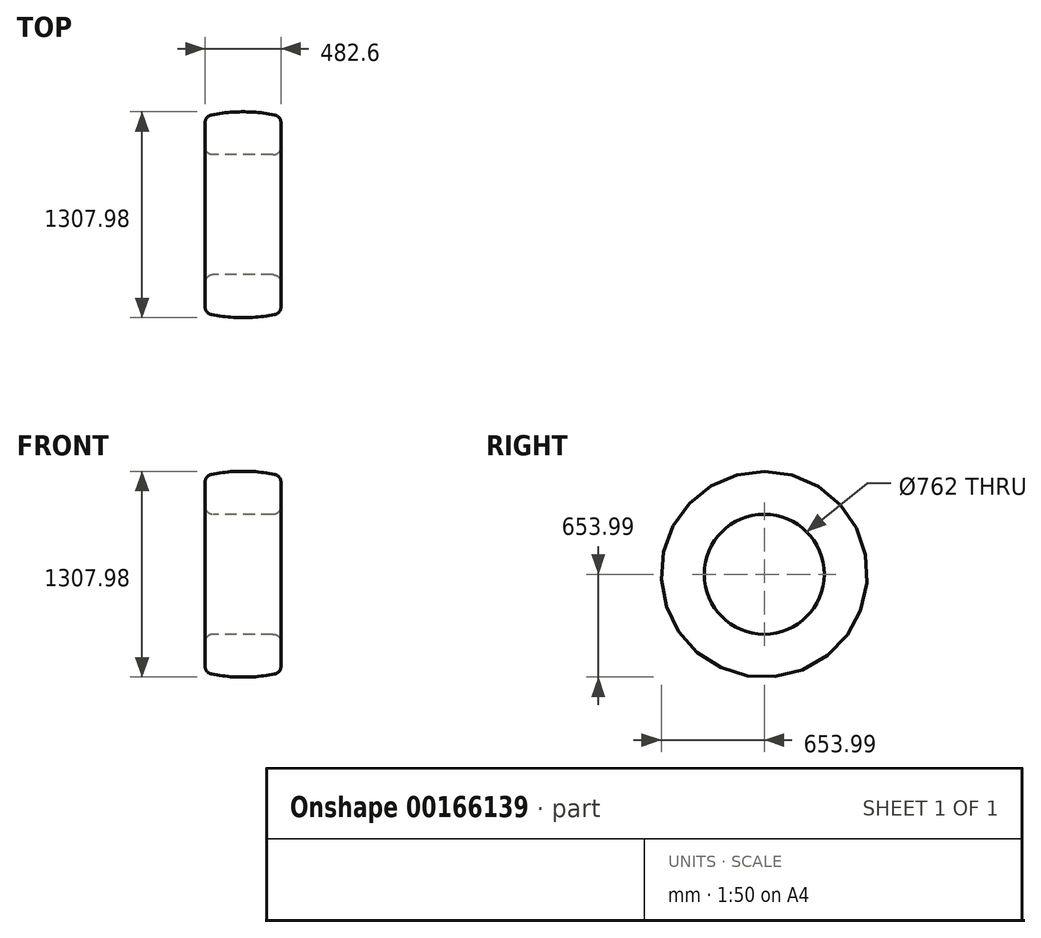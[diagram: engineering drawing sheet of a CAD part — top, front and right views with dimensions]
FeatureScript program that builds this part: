
annotation { "Feature Type Name" : "Feature", "Feature Type Description" : "" }
export const myFeature = defineFeature(function(context is Context, id is Id, definition is map)
    precondition{}
    {
        {
            var Q0;
            Q0=qCreatedBy(makeId("Front.planeOp"),FACE);
            var sketch = newSketch(context, id + "F0", { "sketchPlane" : qUnion([Q0])});
            skLineSegment(sketch, "E0.top", {"start": v(1079.5, -762) * mm, "end": v(1460.5, -762) * mm});
            skLineSegment(sketch, "E0.left", {"start": v(1028.7, -558.8) * mm, "end": v(1028.7, -711.2) * mm});
            skLineSegment(sketch, "E0.right", {"start": v(1511.3, -558.8) * mm, "end": v(1511.3, -711.2) * mm});
            skPoint(sketch, "E1.visualSharp", {"position": v(1028.7, -508) * mm});
            skArc(sketch, "E1.filletArc", {"start": v(1069.47, -509) * mm, "mid": v(1040.2, -526.62) * mm, "end": v(1028.7, -558.8) * mm});
            skArc(sketch, "E2.filletArc", {"start": v(1511.3, -558.8) * mm, "mid": v(1499.8, -526.62) * mm, "end": v(1470.53, -509) * mm});
            skPoint(sketch, "E3.visualSharp", {"position": v(1028.7, -762) * mm});
            skArc(sketch, "E3.filletArc", {"start": v(1028.7, -711.2) * mm, "mid": v(1043.58, -747.12) * mm, "end": v(1079.5, -762) * mm});
            skPoint(sketch, "E4.visualSharp", {"position": v(1511.3, -762) * mm});
            skArc(sketch, "E4.filletArc", {"start": v(1460.5, -762) * mm, "mid": v(1496.42, -747.12) * mm, "end": v(1511.3, -711.2) * mm});
            skArc(sketch, "E5", {"start": v(1470.53, -509) * mm, "mid": v(1270, -489.01) * mm, "end": v(1069.47, -509) * mm});
            skLineSegment(sketch, "E6", {"start": v(-35.67, -1143) * mm, "end": v(726.33, -1143) * mm, "construction": true});
            skSolve(sketch);
        }
        {
            var Q0;
            Q0=makeQuery(id+"F0.imprint","IMPRINT",FACE,{"disambiguationData":[TD([[makeQuery(id+"F0.imprint","IMPRINT",EDGE,{"derivedFrom":sQuery(id+"F0.wireOp",EDGE,"E0.top")}),1.0]])]});
            var Q1;
            Q1=sQuery(id+"F0.wireOp",EDGE,"E6");
            revolve(context, id + "F1", {"entities" : qUnion([Q0]), "axis" : qUnion([Q1]), "revolveType" : RevolveType.FULL});
        }
    });
